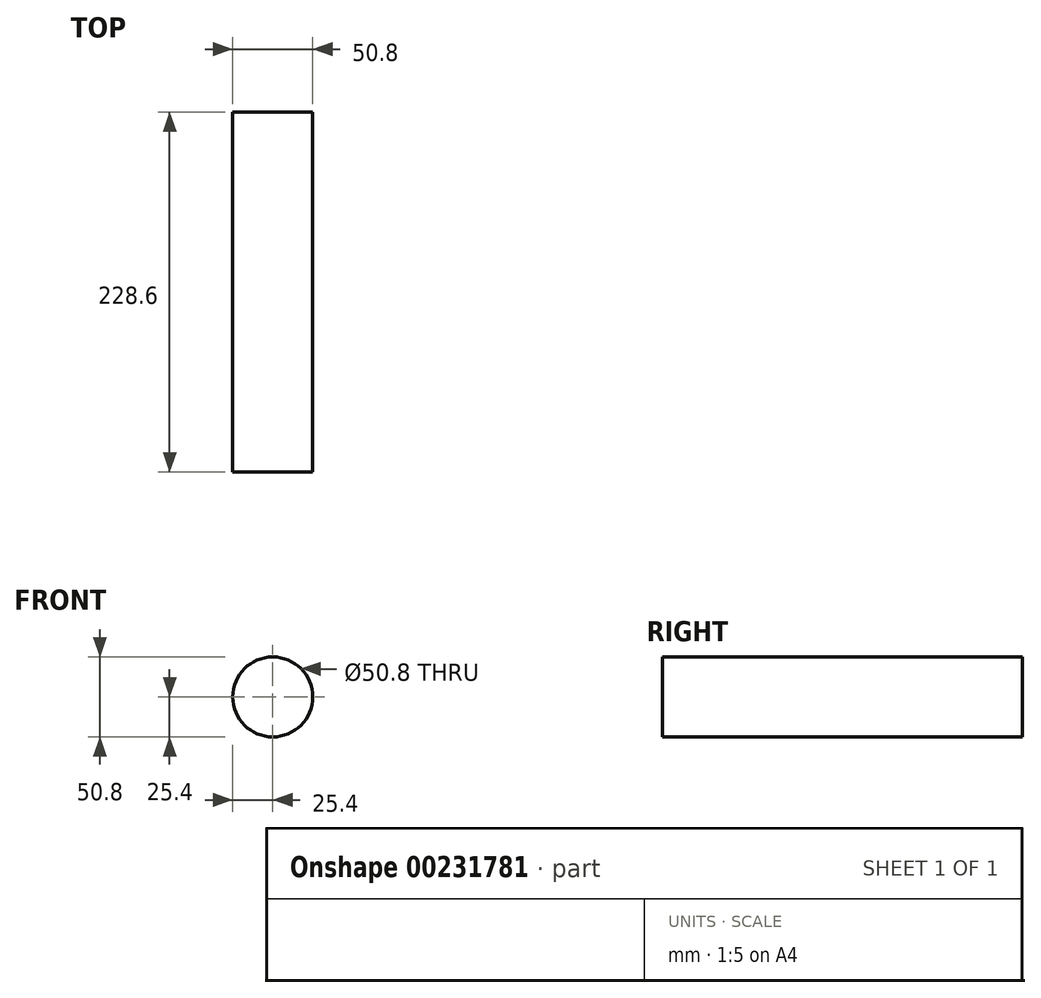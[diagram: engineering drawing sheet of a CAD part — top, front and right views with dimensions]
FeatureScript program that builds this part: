
annotation { "Feature Type Name" : "Feature", "Feature Type Description" : "" }
export const myFeature = defineFeature(function(context is Context, id is Id, definition is map)
    precondition{}
    {
        {
            var Q0;
            Q0=qCreatedBy(makeId("Front.planeOp"),FACE);
            var sketch = newSketch(context, id + "F0", { "sketchPlane" : qUnion([Q0])});
            skCircle(sketch, "E0", {"center": v(0, 0) * mm, "radius": 25.4 * mm});
            skSolve(sketch);
        }
        {
            var Q0;
            Q0 = qSketchRegion(id + "F0", true);
            var Q1;
            Q1=sQuery(id+"F0.wireOp",EDGE,"E0");
            extrude(context, id + "F1", {"entities" : qUnion([Q0]), "bodyType" : ToolBodyType.SURFACE, "surfaceEntities" : qUnion([Q1]), "oppositeDirection" : true, "depth" : 152.4 * mm, "hasSecondDirection" : true, "secondDirectionOppositeDirection" : false, "secondDirectionDepth" : 76.2 * mm});
        }
        {
            var Q0;
            Q0=qCreatedBy(makeId("Right.planeOp"),FACE);
            var sketch = newSketch(context, id + "F2", { "sketchPlane" : qUnion([Q0])});
            skArc(sketch, "E1", {"start": v(136.8, 0) * mm, "mid": v(39, 105.64) * mm, "end": v(-58.78, 0) * mm});
            skSolve(sketch);
        }
        {
            var Q0;
            Q0=qCreatedBy(makeId("Top.planeOp"),FACE);
            var sketch = newSketch(context, id + "F3", { "sketchPlane" : qUnion([Q0])});
            skCircle(sketch, "E2", {"center": v(0, -59.16) * mm, "radius": 5.7 * mm});
            skSolve(sketch);
        }
    });
